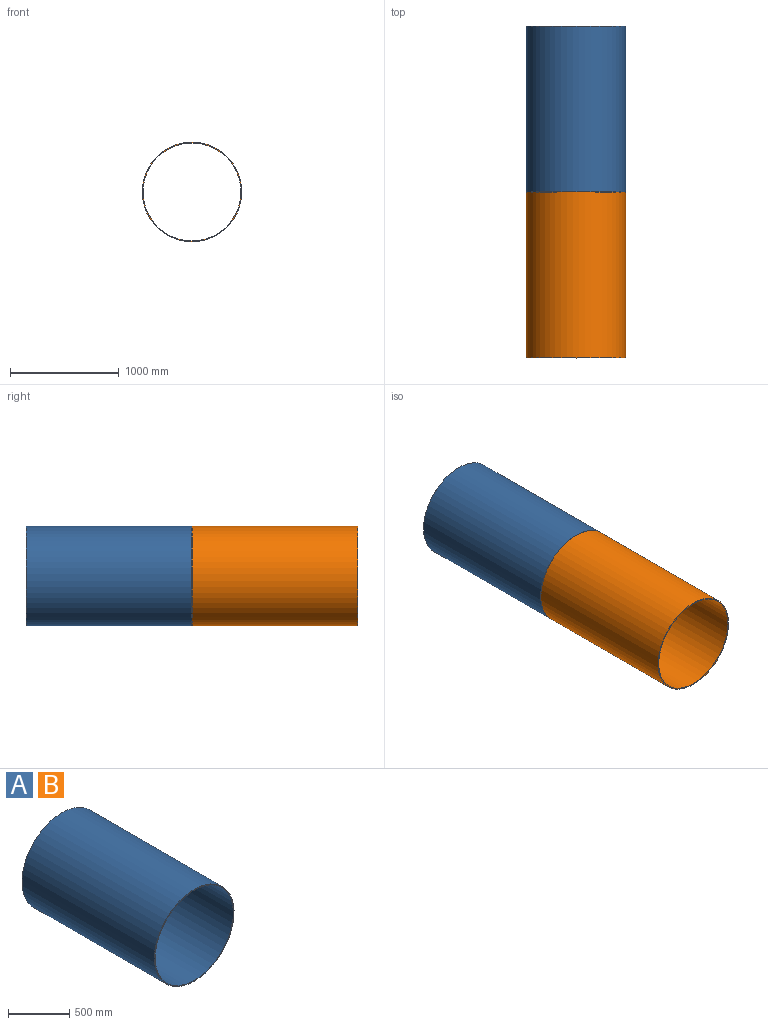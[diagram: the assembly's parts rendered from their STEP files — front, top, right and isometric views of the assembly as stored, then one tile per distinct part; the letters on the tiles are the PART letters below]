
ASSEMBLY  parts=2 mates=2
PART A: 4 faces, bbox 914.4x1524x914.4 mm
  f0: cylinder r=449.26mm len=1524mm, axis (0,1,0), area 4301946.5mm2, adj f2,f3
  f1: cylinder r=457.2mm len=1524mm, axis (0,1,0), area 4377952.6mm2, adj f2,f3
  f2: plane 914.4x914.4mm, normal (0,-1,0), area 22603.9mm2, adj f0,f1
  f3: plane 914.4x914.4mm, normal (0,1,0), area 22603.9mm2, adj f0,f1
PART B: same geometry as A
PLACE A t=(-570.59,2017.12,1888.99)mm
PLACE B t=(-570.59,494.6,1888.99)mm
MATE cylindrical B.f0 <-> A.f0  axis (0,1,0) through (-570.59,494.6,1888.99)mm
MATE planar B.f1 <-> B.f0  axis (0,1,0) through (-570.59,-267.4,1888.99)mm
